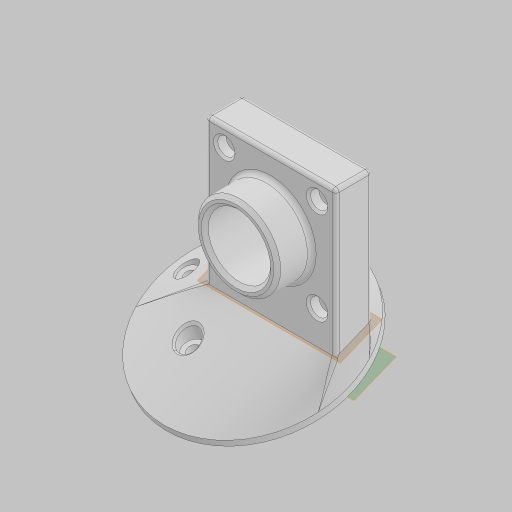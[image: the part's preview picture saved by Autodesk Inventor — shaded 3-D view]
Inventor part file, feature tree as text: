
AUTODESK INVENTOR PART (.ipt)
format: ipt  version: 2023.5 (Build 275446000, 446)  size: 472,064 bytes
history: native  units: in
note: dims shown in document units (in); Inventor stores cm internally (conversion verified against a paired STEP export)
features: extrude x7, hole x3, fillet x3, other x3, projected_geometry x3, plane x2, chamfer x2, loft x1, sketch x1, revolve x1
ambient origin geometry x8: Origin, YZ Plane, XZ Plane, XY Plane, X Axis, Y Axis, Z Axis, Center Point
bodies: Solid1 (feature_tree)
feature tree (26):
  extrude  "Extrusion1"  Depth=0.15in
  extrude  "Extrusion2"  Depth=0.15in TaperAngle=0.0deg
  plane  "Work Plane1"
  extrude  "Extrusion3"  Depth=0.15in
  loft  "Loft1"
  extrude  "Extrusion4"  Depth=0.15in
  hole  "Hole1"  [1 undecoded]
  extrude  "Extrusion5"  Depth=0.15in TaperAngle=0.0deg
  extrude  "Extrusion6"  TaperAngle=0.0deg  [1 undecoded]
  hole  "Hole2"  [1 undecoded]
  plane  "Work Plane2"
  hole  "Hole3"  [1 undecoded]
  fillet  "Fillet1"  Radius=0.3in
  chamfer  "Chamfer1"  Distance=1.1875in
  fillet  "Fillet2"  Radius=0.5in
  extrude  "Extrusion7"  Depth=0.15in
  fillet  "Fillet3"  Radius=1.3386in
  chamfer  "Chamfer2"  Distance=0.15in
  other  "Edges1"
  other  "Edges2"
  projected_geometry  "Projected Loop1"
  projected_geometry  "Projected Loop2"
  sketch  "Sketch11"  dims[d0=1.875in d1=0.525in d2=1.875in d3=0.0in d4=0.4673in d5=1.875in d6=0.0in d7=0.6in d9=2.75in d10=0.1in d11=0.0in d12=0.0in d13=90.0deg d14=0.0in d15=90.0deg d16=1.6in d17=0.3in d18=0.0in d19=0.9in d20=0.75in d21=0.119in d22=0.25in d23=0.6871in d24=1.0in d25=0.8108in d26=1.1875in d27=0.5in d28=0.0in d29=0.1839in d30=1.3386in d31=0.15in d32=0.0in d33=0.094in d34=0.75in d35=0.251in d36=0.15in d37=0.6871in d38=1.0in d39=0.8108in d40=0.9792in d41=0.9792in d42=315.0deg d45=0.177in d46=0.75in d47=0.313in d48=0.45in d49=0.5635in d50=1.0in d51=0.8108in d52=0.05in d53=0.05in d54=0.125in d55=45.0deg d56=0.0625in d57=1.0in d58=1.0in d59=0.0in d60=0.25in d61=0.0312in d62=0.125in d63=45.0deg d64=0.2405in d65=90.0deg]
  other  "Srf1"
  revolve  "RevolutionSrf1"  [1 undecoded]
  projected_geometry  "Project Cut Edges1"
note: 5 required parameter values undecoded (feature->parameter linkage not recoverable at this tier; creation-order binding heuristic only, values carry confidence <= 0.55)